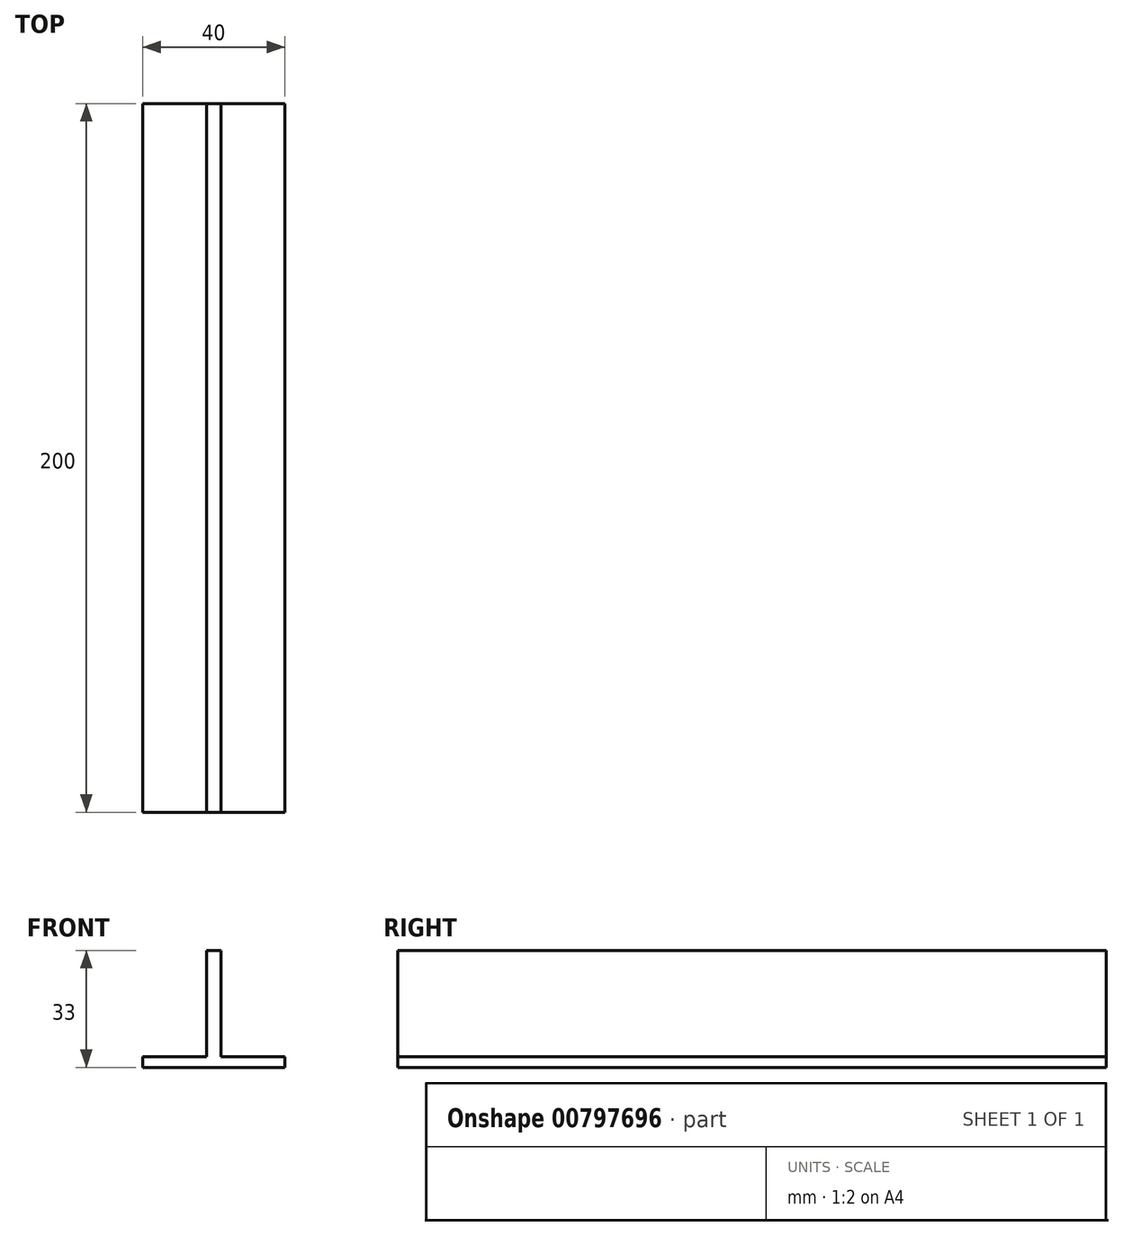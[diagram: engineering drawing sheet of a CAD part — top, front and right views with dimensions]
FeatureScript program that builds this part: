
annotation { "Feature Type Name" : "Feature", "Feature Type Description" : "" }
export const myFeature = defineFeature(function(context is Context, id is Id, definition is map)
    precondition{}
    {
        {
            var Q0;
            Q0=qCreatedBy(makeId("Front.planeOp"),FACE);
            var sketch = newSketch(context, id + "F0", { "sketchPlane" : qUnion([Q0])});
            skLineSegment(sketch, "E0.bottom", {"start": v(-20, 3) * mm, "end": v(20, 3) * mm});
            skLineSegment(sketch, "E0.top", {"start": v(-20, 0) * mm, "end": v(20, 0) * mm});
            skLineSegment(sketch, "E0.left", {"start": v(-20, 3) * mm, "end": v(-20, 0) * mm});
            skLineSegment(sketch, "E0.right", {"start": v(20, 3) * mm, "end": v(20, 0) * mm});
            skLineSegment(sketch, "E1.bottom", {"start": v(-2, 3) * mm, "end": v(2, 3) * mm});
            skLineSegment(sketch, "E1.top", {"start": v(-2, 33) * mm, "end": v(2, 33) * mm});
            skLineSegment(sketch, "E1.left", {"start": v(-2, 3) * mm, "end": v(-2, 33) * mm});
            skLineSegment(sketch, "E1.right", {"start": v(2, 3) * mm, "end": v(2, 33) * mm});
            skSolve(sketch);
        }
        {
            var Q0;
            Q0=makeQuery(id+"F0.imprint","IMPRINT",FACE,{"disambiguationData":[TD([[makeQuery(id+"F0.imprint","IMPRINT",EDGE,{"derivedFrom":sQuery(id+"F0.wireOp",EDGE,"E1.top")}),-1.0]])]});
            var Q1;
            Q1=makeQuery(id+"F0.imprint","IMPRINT",FACE,{"disambiguationData":[TD([[makeQuery(id+"F0.imprint","IMPRINT",EDGE,{"derivedFrom":sQuery(id+"F0.wireOp",EDGE,"E0.top")}),1.0]])]});
            extrude(context, id + "F1", {"entities" : qUnion([Q0, Q1]), "depth" : 200 * mm, "offsetDistance" : 25 * mm});
        }
    });
